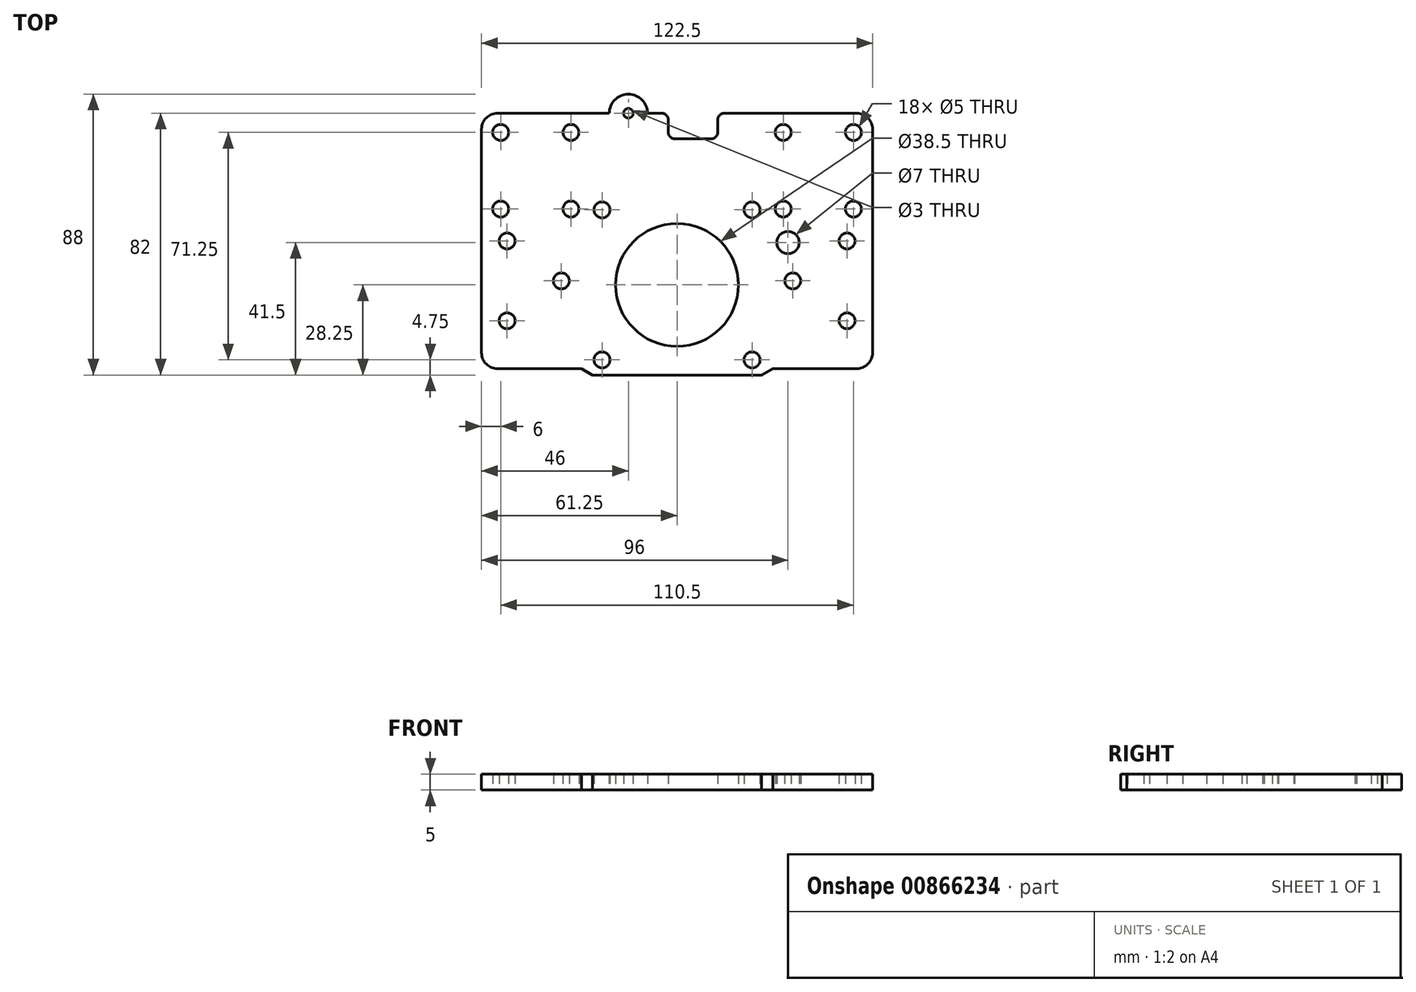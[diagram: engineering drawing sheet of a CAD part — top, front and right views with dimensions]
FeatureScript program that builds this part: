
annotation { "Feature Type Name" : "Feature", "Feature Type Description" : "" }
export const myFeature = defineFeature(function(context is Context, id is Id, definition is map)
    precondition{}
    {
        {
            var Q0;
            Q0=qCreatedBy(makeId("Top.planeOp"),FACE);
            var sketch = newSketch(context, id + "F0", { "sketchPlane" : qUnion([Q0])});
            skCircle(sketch, "E0", {"center": v(0, -15.75) * mm, "radius": 19.25 * mm});
            skCircle(sketch, "E1", {"center": v(-23.5, -39.25) * mm, "radius": 2.5 * mm});
            skCircle(sketch, "E2", {"center": v(-23.5, 7.75) * mm, "radius": 2.5 * mm});
            skCircle(sketch, "E3", {"center": v(23.5, 7.75) * mm, "radius": 2.5 * mm});
            skCircle(sketch, "E4", {"center": v(23.5, -39.25) * mm, "radius": 2.5 * mm});
            skCircle(sketch, "E5", {"center": v(-55.25, 32) * mm, "radius": 2.5 * mm});
            skCircle(sketch, "E6", {"center": v(-33.25, 32) * mm, "radius": 2.5 * mm});
            skCircle(sketch, "E7", {"center": v(-55.25, 8) * mm, "radius": 2.5 * mm});
            skCircle(sketch, "E8", {"center": v(-33.25, 8) * mm, "radius": 2.5 * mm});
            skCircle(sketch, "E9", {"center": v(33.25, 8) * mm, "radius": 2.5 * mm});
            skCircle(sketch, "E10", {"center": v(55.25, 8) * mm, "radius": 2.5 * mm});
            skCircle(sketch, "E11", {"center": v(55.25, 32) * mm, "radius": 2.5 * mm});
            skCircle(sketch, "E12", {"center": v(33.25, 32) * mm, "radius": 2.5 * mm});
            skCircle(sketch, "E13", {"center": v(-53.25, -27) * mm, "radius": 2.5 * mm});
            skCircle(sketch, "E14", {"center": v(-53.25, -2) * mm, "radius": 2.5 * mm});
            skCircle(sketch, "E15", {"center": v(53.25, -27) * mm, "radius": 2.5 * mm});
            skCircle(sketch, "E16", {"center": v(53.25, -2) * mm, "radius": 2.5 * mm});
            skCircle(sketch, "E17", {"center": v(-36.25, -14.5) * mm, "radius": 2.5 * mm});
            skCircle(sketch, "E18", {"center": v(36.25, -14.5) * mm, "radius": 2.5 * mm});
            skCircle(sketch, "E19", {"center": v(34.75, -2.5) * mm, "radius": 3.5 * mm});
            skArc(sketch, "E20", {"start": v(14.75, 38) * mm, "mid": v(13.34, 37.41) * mm, "end": v(12.75, 36) * mm});
            skArc(sketch, "E21", {"start": v(10.75, 30) * mm, "mid": v(12.16, 30.59) * mm, "end": v(12.75, 32) * mm});
            skArc(sketch, "E22", {"start": v(-2.75, 32) * mm, "mid": v(-2.16, 30.59) * mm, "end": v(-0.75, 30) * mm});
            skArc(sketch, "E23", {"start": v(-2.75, 36) * mm, "mid": v(-3.34, 37.41) * mm, "end": v(-4.75, 38) * mm});
            skArc(sketch, "E24", {"start": v(-56.25, 38) * mm, "mid": v(-59.79, 36.54) * mm, "end": v(-61.25, 33) * mm});
            skArc(sketch, "E25", {"start": v(61.25, 33) * mm, "mid": v(59.79, 36.54) * mm, "end": v(56.25, 38) * mm});
            skArc(sketch, "E26", {"start": v(56.25, -42) * mm, "mid": v(59.79, -40.54) * mm, "end": v(61.25, -37) * mm});
            skArc(sketch, "E27", {"start": v(-61.25, -37) * mm, "mid": v(-59.79, -40.54) * mm, "end": v(-56.25, -42) * mm});
            skCircle(sketch, "E28", {"center": v(-15.25, 38) * mm, "radius": 1.5 * mm});
            skArc(sketch, "E29", {"start": v(-9.25, 38) * mm, "mid": v(-15.25, 44) * mm, "end": v(-21.25, 38) * mm});
            skLineSegment(sketch, "E30", {"start": v(-56.25, 38) * mm, "end": v(-21.25, 38) * mm});
            skLineSegment(sketch, "E31", {"start": v(-61.25, 33) * mm, "end": v(-61.25, -37) * mm});
            skLineSegment(sketch, "E32", {"start": v(-56.25, -42) * mm, "end": v(-29.96, -42) * mm});
            skLineSegment(sketch, "E33", {"start": v(61.25, 33) * mm, "end": v(61.25, -37) * mm});
            skLineSegment(sketch, "E34", {"start": v(-26.5, -44) * mm, "end": v(26.5, -44) * mm});
            skLineSegment(sketch, "E35", {"start": v(-26.5, -44) * mm, "end": v(-29.96, -42) * mm});
            skLineSegment(sketch, "E36", {"start": v(26.5, -44) * mm, "end": v(29.96, -42) * mm});
            skLineSegment(sketch, "E37", {"start": v(29.96, -42) * mm, "end": v(56.25, -42) * mm});
            skLineSegment(sketch, "E38", {"start": v(12.75, 36) * mm, "end": v(12.75, 32) * mm});
            skLineSegment(sketch, "E39", {"start": v(-2.75, 36) * mm, "end": v(-2.75, 32) * mm});
            skLineSegment(sketch, "E40", {"start": v(-0.75, 30) * mm, "end": v(10.75, 30) * mm});
            skLineSegment(sketch, "E41", {"start": v(14.75, 38) * mm, "end": v(56.25, 38) * mm});
            skLineSegment(sketch, "E42", {"start": v(-9.25, 38) * mm, "end": v(-4.75, 38) * mm});
            skSolve(sketch);
        }
        {
            var Q0;
            Q0 = qSketchRegion(id + "F0", true);
            extrude(context, id + "F1", {"entities" : qUnion([Q0]), "depth" : 5 * mm, "offsetDistance" : 25 * mm});
        }
    });
